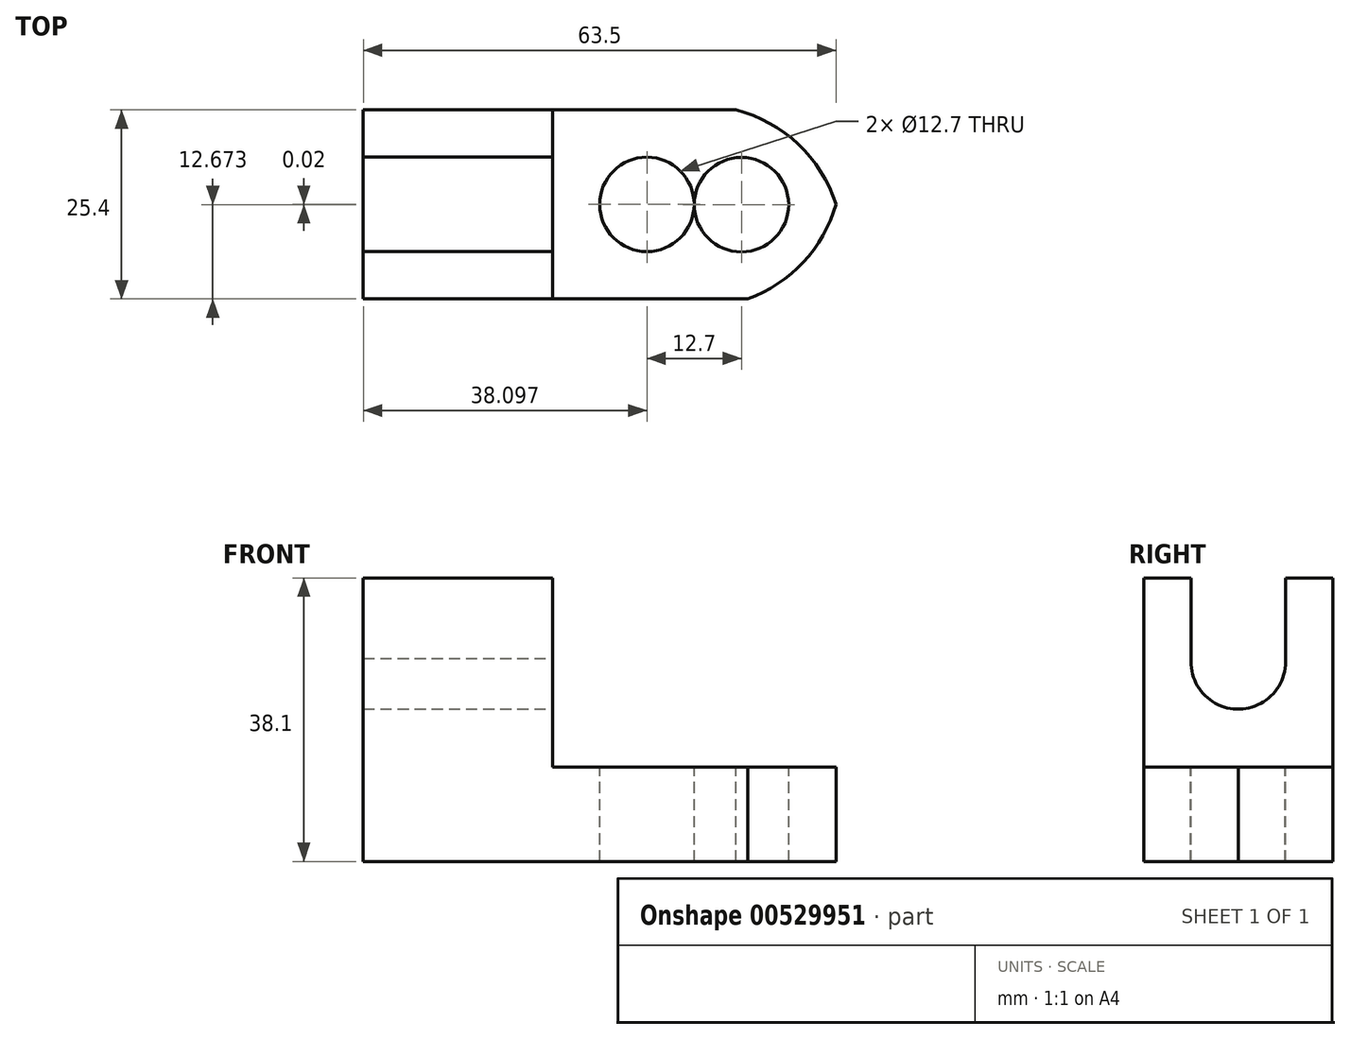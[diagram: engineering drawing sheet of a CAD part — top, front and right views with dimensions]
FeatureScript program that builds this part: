
annotation { "Feature Type Name" : "Feature", "Feature Type Description" : "" }
export const myFeature = defineFeature(function(context is Context, id is Id, definition is map)
    precondition{}
    {
        {
            var Q0;
            Q0=qCreatedBy(makeId("Front.planeOp"),FACE);
            var sketch = newSketch(context, id + "F0", { "sketchPlane" : qUnion([Q0])});
            skLineSegment(sketch, "E0", {"start": v(-76.16, 11.05) * mm, "end": v(-12.66, 11.05) * mm});
            skLineSegment(sketch, "E1", {"start": v(-12.66, 11.05) * mm, "end": v(-12.66, 23.75) * mm});
            skLineSegment(sketch, "E2", {"start": v(-12.66, 23.75) * mm, "end": v(-50.76, 23.75) * mm});
            skLineSegment(sketch, "E3", {"start": v(-50.76, 23.75) * mm, "end": v(-50.76, 49.15) * mm});
            skLineSegment(sketch, "E4", {"start": v(-50.76, 49.15) * mm, "end": v(-76.16, 49.15) * mm});
            skLineSegment(sketch, "E5", {"start": v(-76.16, 49.15) * mm, "end": v(-76.16, 11.05) * mm});
            skSolve(sketch);
        }
        {
            var Q0;
            Q0 = qSketchRegion(id + "F0", true);
            var Q1;
            Q1=makeQuery(id+"F0.imprint","IMPRINT",FACE,{"disambiguationData":[TD([[makeQuery(id+"F0.imprint","IMPRINT",EDGE,{"derivedFrom":sQuery(id+"F0.wireOp",EDGE,"E0")}),1.0]])]});
            extrude(context, id + "F1", {"entities" : qUnion([Q0, Q1]), "depth" : 25.4 * mm, "offsetDistance" : 25.4 * mm});
        }
        {
            var Q0;
            Q0=makeQuery(id+"F1.opExtrude","SWEPT_FACE",FACE,{"disambiguationData":[OSD([sQuery(id+"F0.wireOp",EDGE,"E2")])]});
            var sketch = newSketch(context, id + "F2", { "sketchPlane" : qUnion([Q0])});
            skArc(sketch, "E6", {"start": v(-12.66, -12.7) * mm, "mid": v(-17.73, -4.62) * mm, "end": v(-26.07, 0) * mm});
            skArc(sketch, "E7", {"start": v(-24.53, -25.4) * mm, "mid": v(-17.07, -20.48) * mm, "end": v(-12.66, -12.7) * mm});
            skSolve(sketch);
        }
        {
            var Q0;
            {var subQ0=sQuery(id+"F2.wireOp",EDGE,"E6");Q0=makeQuery(id+"F2.imprint","IMPRINT",FACE,{"disambiguationData":[TD([[makeQuery(id+"F2.imprint","IMPRINT",EDGE,{"derivedFrom":subQ0}),-1.0]])]});}
            var Q1;
            {var subQ0=sQuery(id+"F2.wireOp",EDGE,"E7");Q1=makeQuery(id+"F2.imprint","IMPRINT",FACE,{"disambiguationData":[TD([[makeQuery(id+"F2.imprint","IMPRINT",EDGE,{"derivedFrom":subQ0}),-1.0]])]});}
            extrude(context, id + "F3", {"entities" : qUnion([Q0, Q1]), "operationType" : NewBodyOperationType.REMOVE, "oppositeDirection" : true, "depth" : 25.4 * mm, "offsetDistance" : 25.4 * mm});
        }
        {
            var Q0;
            Q0=makeQuery(id+"F1.opExtrude","SWEPT_FACE",FACE,{"disambiguationData":[OSD([sQuery(id+"F0.wireOp",EDGE,"E2")])]});
            var sketch = newSketch(context, id + "F4", { "sketchPlane" : qUnion([Q0])});
            skCircle(sketch, "E8", {"center": v(-38.06, -12.7) * mm, "radius": 6.35 * mm});
            skCircle(sketch, "E9", {"center": v(-25.36, -12.73) * mm, "radius": 6.35 * mm});
            skSolve(sketch);
        }
        {
            var Q0;
            Q0=makeQuery(id+"F4.imprint","IMPRINT",FACE,{"disambiguationData":[TD([[makeQuery(id+"F4.imprint","IMPRINT",EDGE,{"derivedFrom":sQuery(id+"F4.wireOp",EDGE,"E9")}),1.0]])]});
            var Q1;
            Q1=makeQuery(id+"F4.imprint","IMPRINT",FACE,{"disambiguationData":[TD([[makeQuery(id+"F4.imprint","IMPRINT",EDGE,{"derivedFrom":sQuery(id+"F4.wireOp",EDGE,"E8")}),1.0]])]});
            extrude(context, id + "F5", {"entities" : qUnion([Q0, Q1]), "operationType" : NewBodyOperationType.REMOVE, "oppositeDirection" : true, "depth" : 25.4 * mm, "offsetDistance" : 25.4 * mm});
        }
        {
            var Q0;
            Q0=makeQuery(id+"F1.opExtrude","SWEPT_FACE",FACE,{"disambiguationData":[OSD([sQuery(id+"F0.wireOp",EDGE,"E3")])]});
            var sketch = newSketch(context, id + "F6", { "sketchPlane" : qUnion([Q0])});
            skCircle(sketch, "E10", {"center": v(-12.7, 37.87) * mm, "radius": 6.35 * mm});
            skSolve(sketch);
        }
        {
            var Q0;
            Q0=makeQuery(id+"F6.imprint","IMPRINT",FACE,{"disambiguationData":[TD([[makeQuery(id+"F6.imprint","IMPRINT",EDGE,{"derivedFrom":sQuery(id+"F6.wireOp",EDGE,"E10")}),1.0]])]});
            extrude(context, id + "F7", {"entities" : qUnion([Q0]), "operationType" : NewBodyOperationType.REMOVE, "endBound" : BoundingType.THROUGH_ALL, "oppositeDirection" : true, "depth" : 25.4 * mm, "offsetDistance" : 25.4 * mm});
        }
        {
            var Q0;
            Q0=makeQuery(id+"F1.opExtrude","SWEPT_FACE",FACE,{"disambiguationData":[OSD([sQuery(id+"F0.wireOp",EDGE,"E3")])]});
            var sketch = newSketch(context, id + "F8", { "sketchPlane" : qUnion([Q0])});
            skLineSegment(sketch, "E11", {"start": v(-19.03, 38.35) * mm, "end": v(-19.03, 49.15) * mm});
            skLineSegment(sketch, "E12", {"start": v(-19.03, 49.15) * mm, "end": v(-6.33, 49.15) * mm});
            skLineSegment(sketch, "E13", {"start": v(-6.33, 49.15) * mm, "end": v(-6.35, 37.86) * mm});
            skSolve(sketch);
        }
        {
            var Q0;
            {var subQ0=sQuery(id+"F8.wireOp",EDGE,"E11");Q0=makeQuery(id+"F8.imprint","IMPRINT",FACE,{"disambiguationData":[TD([[makeQuery(id+"F8.imprint","IMPRINT",EDGE,{"derivedFrom":subQ0}),-1.0]])]});}
            extrude(context, id + "F9", {"entities" : qUnion([Q0]), "operationType" : NewBodyOperationType.REMOVE, "oppositeDirection" : true, "depth" : 25.4 * mm, "offsetDistance" : 25.4 * mm});
        }
    });
